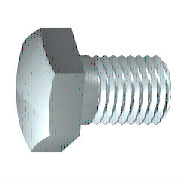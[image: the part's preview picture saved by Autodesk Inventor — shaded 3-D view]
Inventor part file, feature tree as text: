
AUTODESK INVENTOR PART (.ipt)
format: ipt  version: 2020 (Build 240168000, 168)  size: 187,904 bytes
history: native  units: mm (DEFAULTED — no unit token found)
features: sketch x3, extrude x1, chamfer x1, plane x1
ambient origin geometry x7: Origin, YZ Plane, XZ Plane, X Axis, Y Axis, Z Axis, Center Point
bodies: Solid1 (feature_tree), Body (feature_tree)
feature tree (6):
  extrude  "Head"  Depth=57.9mm
  chamfer  "Chamfer1"  Distance=2.4mm
  plane  "Work Plane1"
  sketch  "Sketch1"  dims[d0=60.0mm d1=57.9mm]
  sketch  "Sketch2"  dims[d2=4.0mm]
  sketch  "Sketch4"  dims[d12=90.0deg d3=2.4mm d4=0.0mm d5=30.0deg d21=90.0deg d6=0.429415mm d7=0.429515mm d8=0.0mm d9=0.4001mm d10=5.9mm d11=7.0mm d13=0.429515mm d14=3.621114mm d15=57.9mm d16=0.0mm d19=7.0mm d55=45.0deg d57=0.0mm d58=0.0mm]
